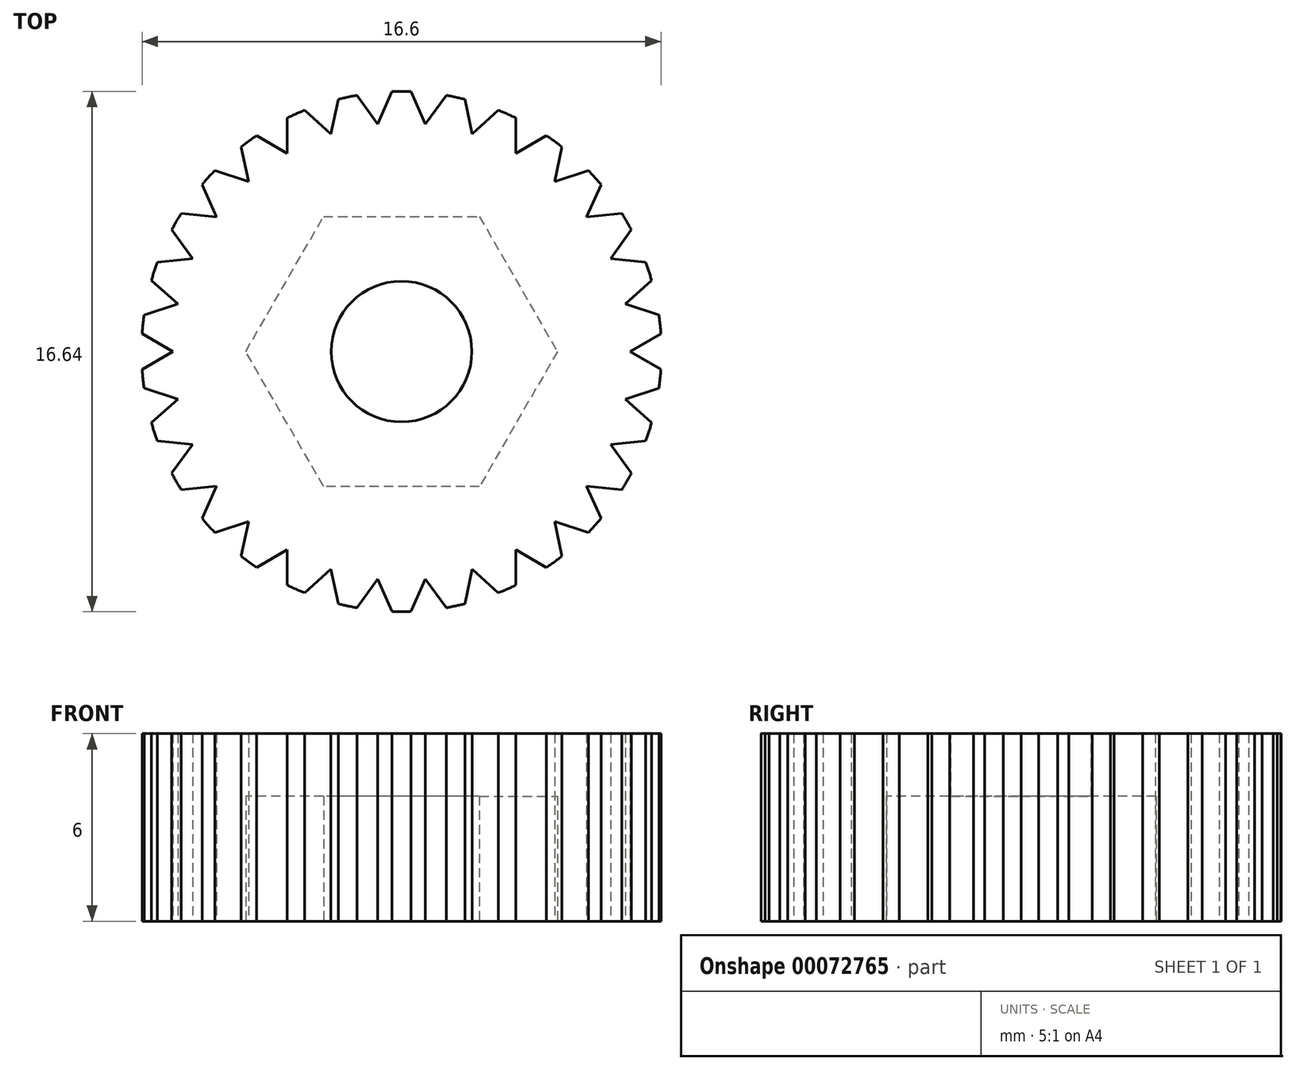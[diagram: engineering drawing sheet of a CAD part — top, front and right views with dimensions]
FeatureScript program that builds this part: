
annotation { "Feature Type Name" : "Feature", "Feature Type Description" : "" }
export const myFeature = defineFeature(function(context is Context, id is Id, definition is map)
    precondition{}
    {
        {
            var Q0;
            Q0=qCreatedBy(makeId("Top.planeOp"),FACE);
            var sketch = newSketch(context, id + "F0", { "sketchPlane" : qUnion([Q0])});
            skCircle(sketch, "E0", {"center": v(0, 0) * mm, "radius": 8.32 * mm});
            skCircle(sketch, "E1.cCircle", {"center": v(0, 0) * mm, "radius": 4.32 * mm, "construction": true});
            skLineSegment(sketch, "E1.0", {"start": v(4.99, 0) * mm, "end": v(2.5, -4.32) * mm});
            skLineSegment(sketch, "E1.1", {"start": v(2.5, -4.32) * mm, "end": v(-2.5, -4.32) * mm});
            skLineSegment(sketch, "E1.2", {"start": v(-2.5, -4.32) * mm, "end": v(-4.99, 0) * mm});
            skLineSegment(sketch, "E1.3", {"start": v(-4.99, 0) * mm, "end": v(-2.5, 4.32) * mm});
            skLineSegment(sketch, "E1.4", {"start": v(-2.5, 4.32) * mm, "end": v(2.5, 4.32) * mm});
            skLineSegment(sketch, "E1.5", {"start": v(2.5, 4.32) * mm, "end": v(4.99, 0) * mm});
            skPoint(sketch, "E1.0.midPoint", {"position": v(3.74, -2.16) * mm});
            skSolve(sketch);
        }
        {
            var Q0;
            Q0=makeQuery(id+"F0.imprint","IMPRINT",FACE,{"disambiguationData":[TD([[makeQuery(id+"F0.imprint","IMPRINT",EDGE,{"derivedFrom":sQuery(id+"F0.wireOp",EDGE,"E0")}),1.0]])]});
            extrude(context, id + "F1", {"entities" : qUnion([Q0]), "depth" : 6 * mm});
        }
        {
            var Q0;
            Q0=makeQuery(id+"F1.opExtrude","CAP_FACE",FACE,{"disambiguationData":[OSD([sQuery(id+"F0.wireOp",EDGE,"E0"),sQuery(id+"F0.wireOp",EDGE,"E1.0"),sQuery(id+"F0.wireOp",EDGE,"E1.1"),sQuery(id+"F0.wireOp",EDGE,"E1.2"),sQuery(id+"F0.wireOp",EDGE,"E1.3"),sQuery(id+"F0.wireOp",EDGE,"E1.4"),sQuery(id+"F0.wireOp",EDGE,"E1.5")])],"isStart":false});
            var sketch = newSketch(context, id + "F2", { "sketchPlane" : qUnion([Q0])});
            skLineSegment(sketch, "E2.0", {"start": v(-2.5, -4.32) * mm, "end": v(-4.99, 0) * mm});
            skLineSegment(sketch, "E3.0", {"start": v(2.5, -4.32) * mm, "end": v(-2.5, -4.32) * mm});
            skLineSegment(sketch, "E4.0", {"start": v(4.99, 0) * mm, "end": v(2.5, -4.32) * mm});
            skLineSegment(sketch, "E5.0", {"start": v(2.5, 4.32) * mm, "end": v(4.99, 0) * mm});
            skLineSegment(sketch, "E6.0", {"start": v(-2.5, 4.32) * mm, "end": v(2.5, 4.32) * mm});
            skLineSegment(sketch, "E7.0", {"start": v(-4.99, 0) * mm, "end": v(-2.5, 4.32) * mm});
            skCircle(sketch, "E8", {"center": v(0, 0) * mm, "radius": 2.25 * mm});
            skSolve(sketch);
        }
        {
            var Q0;
            Q0 = qSketchRegion(id + "F2", true);
            extrude(context, id + "F3", {"entities" : qUnion([Q0]), "operationType" : NewBodyOperationType.ADD, "oppositeDirection" : true, "depth" : 2 * mm});
        }
        {
            var Q0;
            Q0=makeQuery(id+"F1.opExtrude","CAP_FACE",FACE,{"disambiguationData":[OSD([sQuery(id+"F0.wireOp",EDGE,"E0"),sQuery(id+"F0.wireOp",EDGE,"E1.0"),sQuery(id+"F0.wireOp",EDGE,"E1.1"),sQuery(id+"F0.wireOp",EDGE,"E1.2"),sQuery(id+"F0.wireOp",EDGE,"E1.3"),sQuery(id+"F0.wireOp",EDGE,"E1.4"),sQuery(id+"F0.wireOp",EDGE,"E1.5")])],"isStart":true});
            var sketch = newSketch(context, id + "F4", { "sketchPlane" : qUnion([Q0])});
            skLineSegment(sketch, "E9", {"start": v(-9.05, -1) * mm, "end": v(-7.32, 0) * mm});
            skLineSegment(sketch, "E10", {"start": v(-7.32, 0) * mm, "end": v(-9.05, 1) * mm});
            skLineSegment(sketch, "E11", {"start": v(-9.05, 1) * mm, "end": v(-9.05, -1) * mm});
            skLineSegment(sketch, "E12", {"start": v(0, 0) * mm, "end": v(-9.05, 0) * mm, "construction": true});
            skPoint(sketch, "E13.center", {"position": v(0, 0) * mm});
            skLineSegment(sketch, "E13.anchor1", {"start": v(0, 0) * mm, "end": v(-9.05, -1) * mm, "construction": true});
            skLineSegment(sketch, "E13.anchor2", {"start": v(0, 0) * mm, "end": v(-9.05, -1) * mm, "construction": true});
            skSolve(sketch);
        }
        {
            var Q0;
            Q0 = qSketchRegion(id + "F4", true);
            extrude(context, id + "F5", {"entities" : qUnion([Q0]), "oppositeDirection" : true, "depth" : 6 * mm});
        }
        {
            var Q0;
            Q0=makeQuery(id+"F5.opExtrude","SWEPT_BODY",BODY,{"disambiguationData":[OSD([sQuery(id+"F4.wireOp",EDGE,"E9"),sQuery(id+"F4.wireOp",EDGE,"E10"),sQuery(id+"F4.wireOp",EDGE,"E11")])]});
            var Q1;
            Q1=makeQuery(id+"F3.opExtrude","CAP_EDGE",EDGE,{"disambiguationData":[OSD([sQuery(id+"F2.wireOp",EDGE,"E8")])],"isStart":true});
            circularPattern(context, id + "F6", {"entities" : qUnion([Q0]), "axis" : qUnion([Q1]), "angle" : 360 * degree, "instanceCount" : 30, "equalSpace" : true});
        }
        {
            var Q0;
            Q0=makeQuery(id+"F5.opExtrude","SWEPT_BODY",BODY,{"disambiguationData":[OSD([sQuery(id+"F4.wireOp",EDGE,"E9"),sQuery(id+"F4.wireOp",EDGE,"E10"),sQuery(id+"F4.wireOp",EDGE,"E11")])]});
            var Q1;
            Q1=makeQuery(id+"F6.opPattern","COPY",BODY,{"derivedFrom":makeQuery(id+"F5.opExtrude","SWEPT_BODY",BODY,{"disambiguationData":[OSD([sQuery(id+"F4.wireOp",EDGE,"E9"),sQuery(id+"F4.wireOp",EDGE,"E10"),sQuery(id+"F4.wireOp",EDGE,"E11")])]}),"instanceName":"1"});
            var Q2;
            Q2=makeQuery(id+"F6.opPattern","COPY",BODY,{"derivedFrom":makeQuery(id+"F5.opExtrude","SWEPT_BODY",BODY,{"disambiguationData":[OSD([sQuery(id+"F4.wireOp",EDGE,"E9"),sQuery(id+"F4.wireOp",EDGE,"E10"),sQuery(id+"F4.wireOp",EDGE,"E11")])]}),"instanceName":"2"});
            var Q3;
            Q3=makeQuery(id+"F6.opPattern","COPY",BODY,{"derivedFrom":makeQuery(id+"F5.opExtrude","SWEPT_BODY",BODY,{"disambiguationData":[OSD([sQuery(id+"F4.wireOp",EDGE,"E9"),sQuery(id+"F4.wireOp",EDGE,"E10"),sQuery(id+"F4.wireOp",EDGE,"E11")])]}),"instanceName":"3"});
            var Q4;
            Q4=makeQuery(id+"F6.opPattern","COPY",BODY,{"derivedFrom":makeQuery(id+"F5.opExtrude","SWEPT_BODY",BODY,{"disambiguationData":[OSD([sQuery(id+"F4.wireOp",EDGE,"E9"),sQuery(id+"F4.wireOp",EDGE,"E10"),sQuery(id+"F4.wireOp",EDGE,"E11")])]}),"instanceName":"4"});
            var Q5;
            Q5=makeQuery(id+"F6.opPattern","COPY",BODY,{"derivedFrom":makeQuery(id+"F5.opExtrude","SWEPT_BODY",BODY,{"disambiguationData":[OSD([sQuery(id+"F4.wireOp",EDGE,"E9"),sQuery(id+"F4.wireOp",EDGE,"E10"),sQuery(id+"F4.wireOp",EDGE,"E11")])]}),"instanceName":"5"});
            var Q6;
            Q6=makeQuery(id+"F6.opPattern","COPY",BODY,{"derivedFrom":makeQuery(id+"F5.opExtrude","SWEPT_BODY",BODY,{"disambiguationData":[OSD([sQuery(id+"F4.wireOp",EDGE,"E9"),sQuery(id+"F4.wireOp",EDGE,"E10"),sQuery(id+"F4.wireOp",EDGE,"E11")])]}),"instanceName":"6"});
            var Q7;
            Q7=makeQuery(id+"F6.opPattern","COPY",BODY,{"derivedFrom":makeQuery(id+"F5.opExtrude","SWEPT_BODY",BODY,{"disambiguationData":[OSD([sQuery(id+"F4.wireOp",EDGE,"E9"),sQuery(id+"F4.wireOp",EDGE,"E10"),sQuery(id+"F4.wireOp",EDGE,"E11")])]}),"instanceName":"7"});
            var Q8;
            Q8=makeQuery(id+"F6.opPattern","COPY",BODY,{"derivedFrom":makeQuery(id+"F5.opExtrude","SWEPT_BODY",BODY,{"disambiguationData":[OSD([sQuery(id+"F4.wireOp",EDGE,"E9"),sQuery(id+"F4.wireOp",EDGE,"E10"),sQuery(id+"F4.wireOp",EDGE,"E11")])]}),"instanceName":"8"});
            var Q9;
            Q9=makeQuery(id+"F6.opPattern","COPY",BODY,{"derivedFrom":makeQuery(id+"F5.opExtrude","SWEPT_BODY",BODY,{"disambiguationData":[OSD([sQuery(id+"F4.wireOp",EDGE,"E9"),sQuery(id+"F4.wireOp",EDGE,"E10"),sQuery(id+"F4.wireOp",EDGE,"E11")])]}),"instanceName":"9"});
            var Q10;
            Q10=makeQuery(id+"F6.opPattern","COPY",BODY,{"derivedFrom":makeQuery(id+"F5.opExtrude","SWEPT_BODY",BODY,{"disambiguationData":[OSD([sQuery(id+"F4.wireOp",EDGE,"E9"),sQuery(id+"F4.wireOp",EDGE,"E10"),sQuery(id+"F4.wireOp",EDGE,"E11")])]}),"instanceName":"10"});
            var Q11;
            Q11=makeQuery(id+"F6.opPattern","COPY",BODY,{"derivedFrom":makeQuery(id+"F5.opExtrude","SWEPT_BODY",BODY,{"disambiguationData":[OSD([sQuery(id+"F4.wireOp",EDGE,"E9"),sQuery(id+"F4.wireOp",EDGE,"E10"),sQuery(id+"F4.wireOp",EDGE,"E11")])]}),"instanceName":"11"});
            var Q12;
            Q12=makeQuery(id+"F6.opPattern","COPY",BODY,{"derivedFrom":makeQuery(id+"F5.opExtrude","SWEPT_BODY",BODY,{"disambiguationData":[OSD([sQuery(id+"F4.wireOp",EDGE,"E9"),sQuery(id+"F4.wireOp",EDGE,"E10"),sQuery(id+"F4.wireOp",EDGE,"E11")])]}),"instanceName":"12"});
            var Q13;
            Q13=makeQuery(id+"F6.opPattern","COPY",BODY,{"derivedFrom":makeQuery(id+"F5.opExtrude","SWEPT_BODY",BODY,{"disambiguationData":[OSD([sQuery(id+"F4.wireOp",EDGE,"E9"),sQuery(id+"F4.wireOp",EDGE,"E10"),sQuery(id+"F4.wireOp",EDGE,"E11")])]}),"instanceName":"13"});
            var Q14;
            Q14=makeQuery(id+"F6.opPattern","COPY",BODY,{"derivedFrom":makeQuery(id+"F5.opExtrude","SWEPT_BODY",BODY,{"disambiguationData":[OSD([sQuery(id+"F4.wireOp",EDGE,"E9"),sQuery(id+"F4.wireOp",EDGE,"E10"),sQuery(id+"F4.wireOp",EDGE,"E11")])]}),"instanceName":"14"});
            var Q15;
            Q15=makeQuery(id+"F6.opPattern","COPY",BODY,{"derivedFrom":makeQuery(id+"F5.opExtrude","SWEPT_BODY",BODY,{"disambiguationData":[OSD([sQuery(id+"F4.wireOp",EDGE,"E9"),sQuery(id+"F4.wireOp",EDGE,"E10"),sQuery(id+"F4.wireOp",EDGE,"E11")])]}),"instanceName":"15"});
            var Q16;
            Q16=makeQuery(id+"F6.opPattern","COPY",BODY,{"derivedFrom":makeQuery(id+"F5.opExtrude","SWEPT_BODY",BODY,{"disambiguationData":[OSD([sQuery(id+"F4.wireOp",EDGE,"E9"),sQuery(id+"F4.wireOp",EDGE,"E10"),sQuery(id+"F4.wireOp",EDGE,"E11")])]}),"instanceName":"16"});
            var Q17;
            Q17=makeQuery(id+"F6.opPattern","COPY",BODY,{"derivedFrom":makeQuery(id+"F5.opExtrude","SWEPT_BODY",BODY,{"disambiguationData":[OSD([sQuery(id+"F4.wireOp",EDGE,"E9"),sQuery(id+"F4.wireOp",EDGE,"E10"),sQuery(id+"F4.wireOp",EDGE,"E11")])]}),"instanceName":"17"});
            var Q18;
            Q18=makeQuery(id+"F6.opPattern","COPY",BODY,{"derivedFrom":makeQuery(id+"F5.opExtrude","SWEPT_BODY",BODY,{"disambiguationData":[OSD([sQuery(id+"F4.wireOp",EDGE,"E9"),sQuery(id+"F4.wireOp",EDGE,"E10"),sQuery(id+"F4.wireOp",EDGE,"E11")])]}),"instanceName":"18"});
            var Q19;
            Q19=makeQuery(id+"F6.opPattern","COPY",BODY,{"derivedFrom":makeQuery(id+"F5.opExtrude","SWEPT_BODY",BODY,{"disambiguationData":[OSD([sQuery(id+"F4.wireOp",EDGE,"E9"),sQuery(id+"F4.wireOp",EDGE,"E10"),sQuery(id+"F4.wireOp",EDGE,"E11")])]}),"instanceName":"19"});
            var Q20;
            Q20=makeQuery(id+"F6.opPattern","COPY",BODY,{"derivedFrom":makeQuery(id+"F5.opExtrude","SWEPT_BODY",BODY,{"disambiguationData":[OSD([sQuery(id+"F4.wireOp",EDGE,"E9"),sQuery(id+"F4.wireOp",EDGE,"E10"),sQuery(id+"F4.wireOp",EDGE,"E11")])]}),"instanceName":"20"});
            var Q21;
            Q21=makeQuery(id+"F6.opPattern","COPY",BODY,{"derivedFrom":makeQuery(id+"F5.opExtrude","SWEPT_BODY",BODY,{"disambiguationData":[OSD([sQuery(id+"F4.wireOp",EDGE,"E9"),sQuery(id+"F4.wireOp",EDGE,"E10"),sQuery(id+"F4.wireOp",EDGE,"E11")])]}),"instanceName":"21"});
            var Q22;
            Q22=makeQuery(id+"F6.opPattern","COPY",BODY,{"derivedFrom":makeQuery(id+"F5.opExtrude","SWEPT_BODY",BODY,{"disambiguationData":[OSD([sQuery(id+"F4.wireOp",EDGE,"E9"),sQuery(id+"F4.wireOp",EDGE,"E10"),sQuery(id+"F4.wireOp",EDGE,"E11")])]}),"instanceName":"22"});
            var Q23;
            Q23=makeQuery(id+"F6.opPattern","COPY",BODY,{"derivedFrom":makeQuery(id+"F5.opExtrude","SWEPT_BODY",BODY,{"disambiguationData":[OSD([sQuery(id+"F4.wireOp",EDGE,"E9"),sQuery(id+"F4.wireOp",EDGE,"E10"),sQuery(id+"F4.wireOp",EDGE,"E11")])]}),"instanceName":"23"});
            var Q24;
            Q24=makeQuery(id+"F6.opPattern","COPY",BODY,{"derivedFrom":makeQuery(id+"F5.opExtrude","SWEPT_BODY",BODY,{"disambiguationData":[OSD([sQuery(id+"F4.wireOp",EDGE,"E9"),sQuery(id+"F4.wireOp",EDGE,"E10"),sQuery(id+"F4.wireOp",EDGE,"E11")])]}),"instanceName":"24"});
            var Q25;
            Q25=makeQuery(id+"F6.opPattern","COPY",BODY,{"derivedFrom":makeQuery(id+"F5.opExtrude","SWEPT_BODY",BODY,{"disambiguationData":[OSD([sQuery(id+"F4.wireOp",EDGE,"E9"),sQuery(id+"F4.wireOp",EDGE,"E10"),sQuery(id+"F4.wireOp",EDGE,"E11")])]}),"instanceName":"25"});
            var Q26;
            Q26=makeQuery(id+"F6.opPattern","COPY",BODY,{"derivedFrom":makeQuery(id+"F5.opExtrude","SWEPT_BODY",BODY,{"disambiguationData":[OSD([sQuery(id+"F4.wireOp",EDGE,"E9"),sQuery(id+"F4.wireOp",EDGE,"E10"),sQuery(id+"F4.wireOp",EDGE,"E11")])]}),"instanceName":"26"});
            var Q27;
            Q27=makeQuery(id+"F6.opPattern","COPY",BODY,{"derivedFrom":makeQuery(id+"F5.opExtrude","SWEPT_BODY",BODY,{"disambiguationData":[OSD([sQuery(id+"F4.wireOp",EDGE,"E9"),sQuery(id+"F4.wireOp",EDGE,"E10"),sQuery(id+"F4.wireOp",EDGE,"E11")])]}),"instanceName":"27"});
            var Q28;
            Q28=makeQuery(id+"F6.opPattern","COPY",BODY,{"derivedFrom":makeQuery(id+"F5.opExtrude","SWEPT_BODY",BODY,{"disambiguationData":[OSD([sQuery(id+"F4.wireOp",EDGE,"E9"),sQuery(id+"F4.wireOp",EDGE,"E10"),sQuery(id+"F4.wireOp",EDGE,"E11")])]}),"instanceName":"28"});
            var Q29;
            Q29=makeQuery(id+"F6.opPattern","COPY",BODY,{"derivedFrom":makeQuery(id+"F5.opExtrude","SWEPT_BODY",BODY,{"disambiguationData":[OSD([sQuery(id+"F4.wireOp",EDGE,"E9"),sQuery(id+"F4.wireOp",EDGE,"E10"),sQuery(id+"F4.wireOp",EDGE,"E11")])]}),"instanceName":"29"});
            var Q30;
            Q30=makeQuery(id+"F1.opExtrude","SWEPT_BODY",BODY,{"disambiguationData":[OSD([sQuery(id+"F0.wireOp",EDGE,"E0"),sQuery(id+"F0.wireOp",EDGE,"E1.0"),sQuery(id+"F0.wireOp",EDGE,"E1.1"),sQuery(id+"F0.wireOp",EDGE,"E1.2"),sQuery(id+"F0.wireOp",EDGE,"E1.3"),sQuery(id+"F0.wireOp",EDGE,"E1.4"),sQuery(id+"F0.wireOp",EDGE,"E1.5")])]});
            booleanBodies(context, id + "F7", {"operationType" : BooleanOperationType.SUBTRACTION, "tools" : qUnion([Q0, Q1, Q2, Q3, Q4, Q5, Q6, Q7, Q8, Q9, Q10, Q11, Q12, Q13, Q14, Q15, Q16, Q17, Q18, Q19, Q20, Q21, Q22, Q23, Q24, Q25, Q26, Q27, Q28, Q29]), "targets" : qUnion([Q30])});
        }
    });
